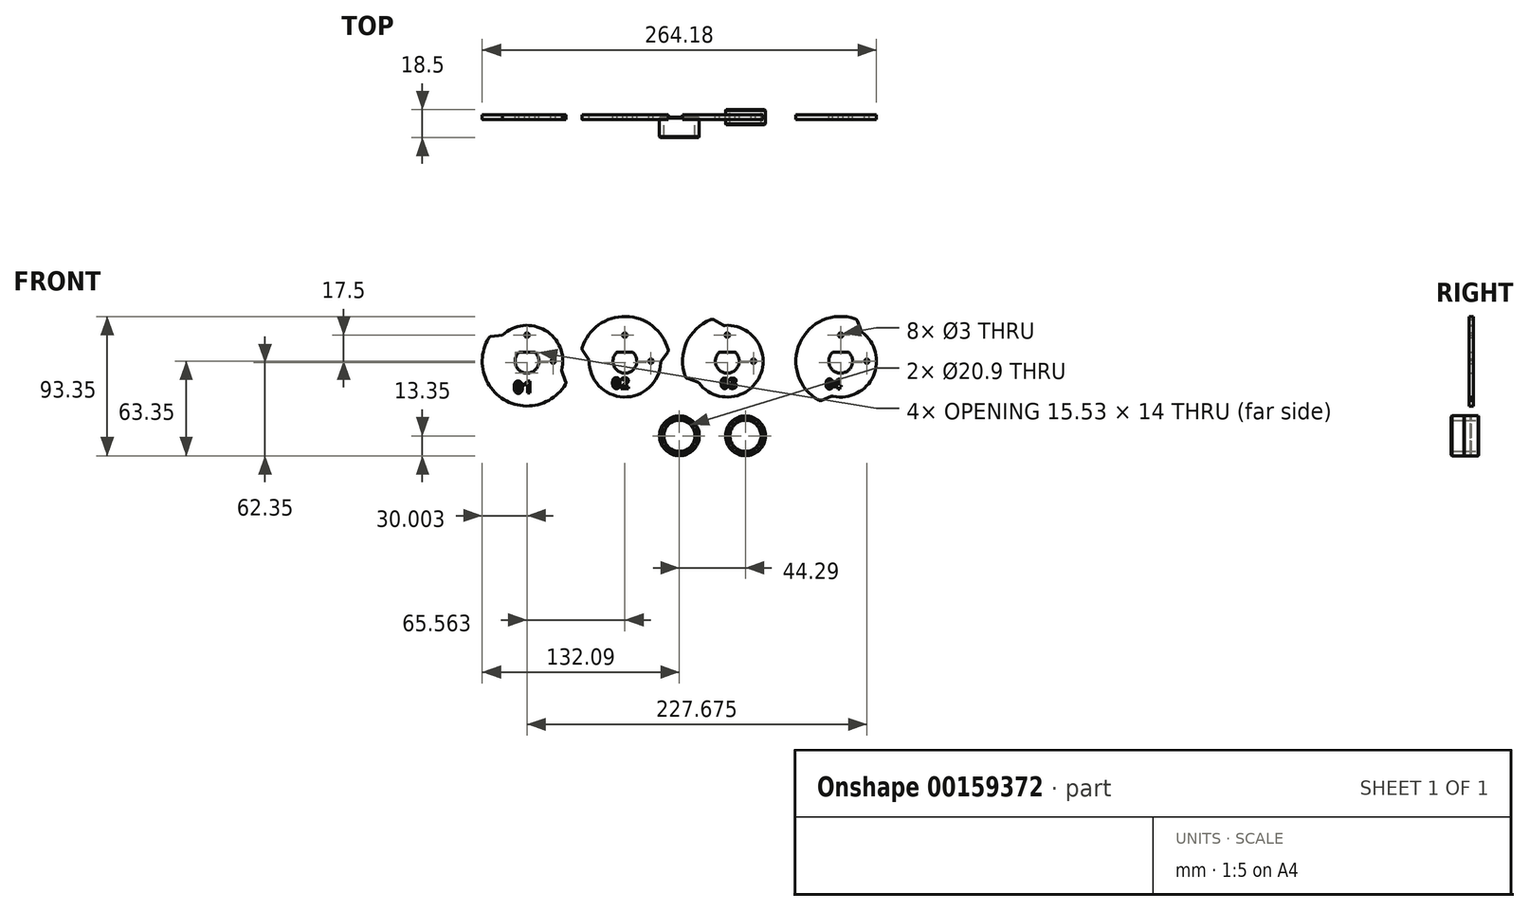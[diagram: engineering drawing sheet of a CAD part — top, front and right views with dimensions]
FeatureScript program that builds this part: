
annotation { "Feature Type Name" : "Feature", "Feature Type Description" : "" }
export const myFeature = defineFeature(function(context is Context, id is Id, definition is map)
    precondition{}
    {
        {
            var Q0;
            Q0=qCreatedBy(makeId("Front.planeOp"),FACE);
            var sketch = newSketch(context, id + "F0", { "sketchPlane" : qUnion([Q0])});
            skArc(sketch, "E0", {"start": v(21.15, 27.93) * mm, "mid": v(4.75, 12.31) * mm, "end": v(3.94, -10.32) * mm});
            skArc(sketch, "E1", {"start": v(3.94, -10.32) * mm, "mid": v(4.41, -11.06) * mm, "end": v(5.16, -11.52) * mm});
            skLineSegment(sketch, "E2", {"start": v(5.16, -11.52) * mm, "end": v(12.1, -13.91) * mm});
            skArc(sketch, "E3", {"start": v(12.1, -13.91) * mm, "mid": v(12.63, -14.18) * mm, "end": v(13.05, -14.59) * mm});
            skArc(sketch, "E4", {"start": v(13.05, -14.59) * mm, "mid": v(54, -9.85) * mm, "end": v(30.39, 23.94) * mm});
            skArc(sketch, "E5", {"start": v(30.39, 23.94) * mm, "mid": v(29.8, 23.98) * mm, "end": v(29.26, 24.2) * mm});
            skLineSegment(sketch, "E6", {"start": v(29.26, 24.2) * mm, "end": v(22.86, 27.8) * mm});
            skArc(sketch, "E7", {"start": v(22.86, 27.8) * mm, "mid": v(22.02, 28.06) * mm, "end": v(21.15, 27.93) * mm});
            skCircle(sketch, "E8", {"center": v(32.1, 17.5) * mm, "radius": 1.5 * mm});
            skCircle(sketch, "E9", {"center": v(49.6, 0) * mm, "radius": 1.5 * mm});
            skArc(sketch, "E10", {"start": v(103.07, -23.47) * mm, "mid": v(129.97, -9.85) * mm, "end": v(122.33, 19.32) * mm});
            skArc(sketch, "E11", {"start": v(122.33, 19.32) * mm, "mid": v(121.91, 19.73) * mm, "end": v(121.63, 20.24) * mm});
            skLineSegment(sketch, "E12", {"start": v(121.63, 20.24) * mm, "end": v(119.12, 27.15) * mm});
            skArc(sketch, "E13", {"start": v(119.12, 27.15) * mm, "mid": v(118.64, 27.89) * mm, "end": v(117.9, 28.35) * mm});
            skArc(sketch, "E14", {"start": v(117.9, 28.35) * mm, "mid": v(80.73, 12.31) * mm, "end": v(93.37, -26.14) * mm});
            skArc(sketch, "E15", {"start": v(93.37, -26.14) * mm, "mid": v(94.21, -26.4) * mm, "end": v(95.09, -26.26) * mm});
            skLineSegment(sketch, "E16", {"start": v(95.09, -26.26) * mm, "end": v(101.92, -23.57) * mm});
            skArc(sketch, "E17", {"start": v(101.92, -23.57) * mm, "mid": v(102.49, -23.43) * mm, "end": v(103.07, -23.47) * mm});
            skCircle(sketch, "E18", {"center": v(108.09, 17.5) * mm, "radius": 1.5 * mm});
            skCircle(sketch, "E19", {"center": v(125.59, 0) * mm, "radius": 1.5 * mm});
            skArc(sketch, "E20", {"start": v(-60.52, 0.62) * mm, "mid": v(-37.34, -23.99) * mm, "end": v(-12.55, -1) * mm});
            skArc(sketch, "E21", {"start": v(-12.17, 0.09) * mm, "mid": v(-12.44, -0.43) * mm, "end": v(-12.55, -1) * mm});
            skLineSegment(sketch, "E22", {"start": v(-12.17, 0.09) * mm, "end": v(-7.85, 6.03) * mm});
            skArc(sketch, "E23", {"start": v(-7.85, 6.03) * mm, "mid": v(-7.5, 6.84) * mm, "end": v(-7.54, 7.72) * mm});
            skArc(sketch, "E24", {"start": v(-7.54, 7.72) * mm, "mid": v(-35.88, 30) * mm, "end": v(-65.16, 8.96) * mm});
            skArc(sketch, "E25", {"start": v(-65.16, 8.96) * mm, "mid": v(-65.23, 8.08) * mm, "end": v(-64.91, 7.26) * mm});
            skLineSegment(sketch, "E26", {"start": v(-64.91, 7.26) * mm, "end": v(-60.52, 0.62) * mm});
            skCircle(sketch, "E27", {"center": v(-36.52, 17.5) * mm, "radius": 1.5 * mm});
            skCircle(sketch, "E28", {"center": v(-19.02, 0) * mm, "radius": 1.5 * mm});
            skLineSegment(sketch, "E29", {"start": v(-118.46, 17.55) * mm, "end": v(-126.35, 16.44) * mm});
            skArc(sketch, "E30", {"start": v(-127.78, 15.49) * mm, "mid": v(-117.53, -25.72) * mm, "end": v(-76.34, -15.4) * mm});
            skArc(sketch, "E31", {"start": v(-126.35, 16.44) * mm, "mid": v(-127.17, 16.12) * mm, "end": v(-127.78, 15.49) * mm});
            skArc(sketch, "E32", {"start": v(-76.34, -15.4) * mm, "mid": v(-76.06, -14.56) * mm, "end": v(-76.18, -13.68) * mm});
            skLineSegment(sketch, "E33", {"start": v(-76.18, -13.68) * mm, "end": v(-78.8, -6.5) * mm});
            skArc(sketch, "E34", {"start": v(-78.83, -5.9) * mm, "mid": v(-78.86, -6.2) * mm, "end": v(-78.8, -6.5) * mm});
            skArc(sketch, "E35", {"start": v(-78.83, -5.9) * mm, "mid": v(-89.87, 20.65) * mm, "end": v(-118.46, 17.55) * mm});
            skCircle(sketch, "E36", {"center": v(-102.09, 17.5) * mm, "radius": 1.5 * mm});
            skCircle(sketch, "E37", {"center": v(-84.59, 0) * mm, "radius": 1.5 * mm});
            skArc(sketch, "E38", {"start": v(-96.8, 6) * mm, "mid": v(-102.09, -8) * mm, "end": v(-107.38, 6) * mm});
            skLineSegment(sketch, "E39", {"start": v(-107.38, 6) * mm, "end": v(-96.8, 6) * mm});
            skArc(sketch, "E40", {"start": v(-31.23, 6) * mm, "mid": v(-36.52, -8) * mm, "end": v(-41.82, 6) * mm});
            skLineSegment(sketch, "E41", {"start": v(-41.82, 6) * mm, "end": v(-31.23, 6) * mm});
            skArc(sketch, "E42", {"start": v(37.4, 6) * mm, "mid": v(32.1, -8) * mm, "end": v(26.81, 6) * mm});
            skLineSegment(sketch, "E43", {"start": v(26.81, 6) * mm, "end": v(37.4, 6) * mm});
            skArc(sketch, "E44", {"start": v(113.38, 6) * mm, "mid": v(108.09, -8) * mm, "end": v(102.8, 6) * mm});
            skLineSegment(sketch, "E45", {"start": v(102.8, 6) * mm, "end": v(113.38, 6) * mm});
            skSolve(sketch);
        }
        {
            var Q0;
            Q0=makeQuery(id+"F0.imprint","IMPRINT",FACE,{"disambiguationData":[TD([[makeQuery(id+"F0.imprint","IMPRINT",EDGE,{"derivedFrom":sQuery(id+"F0.wireOp",EDGE,"E29")}),1.0]])]});
            var Q1;
            Q1=makeQuery(id+"F0.imprint","IMPRINT",FACE,{"disambiguationData":[TD([[makeQuery(id+"F0.imprint","IMPRINT",EDGE,{"derivedFrom":sQuery(id+"F0.wireOp",EDGE,"E20")}),1.0]])]});
            var Q2;
            Q2=makeQuery(id+"F0.imprint","IMPRINT",FACE,{"disambiguationData":[TD([[makeQuery(id+"F0.imprint","IMPRINT",EDGE,{"derivedFrom":sQuery(id+"F0.wireOp",EDGE,"E0")}),1.0]])]});
            var Q3;
            Q3=makeQuery(id+"F0.imprint","IMPRINT",FACE,{"disambiguationData":[TD([[makeQuery(id+"F0.imprint","IMPRINT",EDGE,{"derivedFrom":sQuery(id+"F0.wireOp",EDGE,"E10")}),1.0]])]});
            extrude(context, id + "F1", {"entities" : qUnion([Q0, Q1, Q2, Q3]), "depth" : 3 * mm, "symmetric" : true});
        }
        {
            var Q0;
            Q0=makeQuery(id+"F1.opExtrude","CAP_FACE",FACE,{"disambiguationData":[OSD([sQuery(id+"F0.wireOp",EDGE,"E29"),sQuery(id+"F0.wireOp",EDGE,"E30"),sQuery(id+"F0.wireOp",EDGE,"E31"),sQuery(id+"F0.wireOp",EDGE,"E32"),sQuery(id+"F0.wireOp",EDGE,"E33"),sQuery(id+"F0.wireOp",EDGE,"E34"),sQuery(id+"F0.wireOp",EDGE,"E35"),sQuery(id+"F0.wireOp",EDGE,"E36"),sQuery(id+"F0.wireOp",EDGE,"E37"),sQuery(id+"F0.wireOp",EDGE,"E38"),sQuery(id+"F0.wireOp",EDGE,"E39")])],"isStart":false});
            var sketch = newSketch(context, id + "F2", { "sketchPlane" : qUnion([Q0])});
            skText(sketch, "E46", { "text": "01", "fontName": "OpenSans-Bold.ttf"});
            skText(sketch, "E47", { "text": "02", "fontName": "OpenSans-Bold.ttf"});
            skText(sketch, "E48", { "text": "03", "fontName": "OpenSans-Bold.ttf"});
            skText(sketch, "E49", { "text": "04\n", "fontName": "OpenSans-Bold.ttf"});
            const initialGuessF2  = {"E46": [-0.11114, -0.02139, 1, 0, 0.00803], "E47": [-0.04517, -0.01826, 1, 0, 0.00723], "E48": [0.0276, -0.0182, 1, 0, 0.00688], "E49": [0.0979, -0.01859, 1, 0, 0.00668]};
            skSetInitialGuess(sketch, initialGuessF2);
            skSolve(sketch);
        }
        {
            var Q0;
            Q0=qSketchRegion(id+"F2",true);
            extrude(context, id + "F3", {"entities" : qUnion([Q0]), "operationType" : NewBodyOperationType.REMOVE, "oppositeDirection" : true, "depth" : 0.3 * mm});
        }
        {
            var Q0;
            Q0=qCreatedBy(makeId("Front.planeOp"),FACE);
            var sketch = newSketch(context, id + "F4", { "sketchPlane" : qUnion([Q0])});
            skCircle(sketch, "E50", {"center": v(0, -50) * mm, "radius": 10.45 * mm});
            skCircle(sketch, "E51", {"center": v(0, -50) * mm, "radius": 13.35 * mm});
            skSolve(sketch);
        }
        {
            var Q0;
            Q0=makeQuery(id+"F4.imprint","IMPRINT",FACE,{"disambiguationData":[TD([[makeQuery(id+"F4.imprint","IMPRINT",EDGE,{"derivedFrom":sQuery(id+"F4.wireOp",EDGE,"E50")}),-1.0]])]});
            extrude(context, id + "F5", {"entities" : qUnion([Q0]), "depth" : 13.5 * mm});
        }
        {
            var Q0;
            Q0=makeQuery(id+"F5.opExtrude","CAP_EDGE",EDGE,{"disambiguationData":[OSD([sQuery(id+"F4.wireOp",EDGE,"E50")])],"isStart":false});
            var Q1;
            Q1=makeQuery(id+"F5.opExtrude","CAP_EDGE",EDGE,{"disambiguationData":[OSD([sQuery(id+"F4.wireOp",EDGE,"E51")])],"isStart":false});
            var Q2;
            Q2=makeQuery(id+"F5.opExtrude","CAP_EDGE",EDGE,{"disambiguationData":[OSD([sQuery(id+"F4.wireOp",EDGE,"E50")])],"isStart":true});
            var Q3;
            Q3=makeQuery(id+"F5.opExtrude","CAP_EDGE",EDGE,{"disambiguationData":[OSD([sQuery(id+"F4.wireOp",EDGE,"E51")])],"isStart":true});
            chamfer(context, id + "F6", {"entities" : qUnion([Q0, Q1, Q2, Q3]), "width" : 0.5 * mm, "tangentPropagation" : true});
        }
        {
            var Q0;
            Q0=qCreatedBy(makeId("Front.planeOp"),FACE);
            var sketch = newSketch(context, id + "F7", { "sketchPlane" : qUnion([Q0])});
            skCircle(sketch, "E52.0", {"center": v(0, -50) * mm, "radius": 13.35 * mm, "construction": true});
            skCircle(sketch, "E53.0", {"center": v(0, -50) * mm, "radius": 10.45 * mm, "construction": true});
            skCircle(sketch, "E54", {"center": v(44.29, -50) * mm, "radius": 13.35 * mm});
            skCircle(sketch, "E55", {"center": v(44.29, -50) * mm, "radius": 10.45 * mm});
            skSolve(sketch);
        }
        {
            var Q0;
            Q0=makeQuery(id+"F7.imprint","IMPRINT",FACE,{"disambiguationData":[TD([[makeQuery(id+"F7.imprint","IMPRINT",EDGE,{"derivedFrom":sQuery(id+"F7.wireOp",EDGE,"E54")}),1.0]])]});
            extrude(context, id + "F8", {"entities" : qUnion([Q0]), "depth" : 10 * mm, "symmetric" : true});
        }
        {
            var Q0;
            Q0=makeQuery(id+"F8.opExtrude","CAP_EDGE",EDGE,{"disambiguationData":[OSD([sQuery(id+"F7.wireOp",EDGE,"E55")])],"isStart":false});
            var Q1;
            Q1=makeQuery(id+"F8.opExtrude","CAP_EDGE",EDGE,{"disambiguationData":[OSD([sQuery(id+"F7.wireOp",EDGE,"E54")])],"isStart":false});
            var Q2;
            Q2=makeQuery(id+"F8.opExtrude","CAP_EDGE",EDGE,{"disambiguationData":[OSD([sQuery(id+"F7.wireOp",EDGE,"E54")])],"isStart":true});
            var Q3;
            Q3=makeQuery(id+"F8.opExtrude","CAP_EDGE",EDGE,{"disambiguationData":[OSD([sQuery(id+"F7.wireOp",EDGE,"E55")])],"isStart":true});
            chamfer(context, id + "F9", {"entities" : qUnion([Q0, Q1, Q2, Q3]), "width" : 0.5 * mm, "tangentPropagation" : true});
        }
    });
